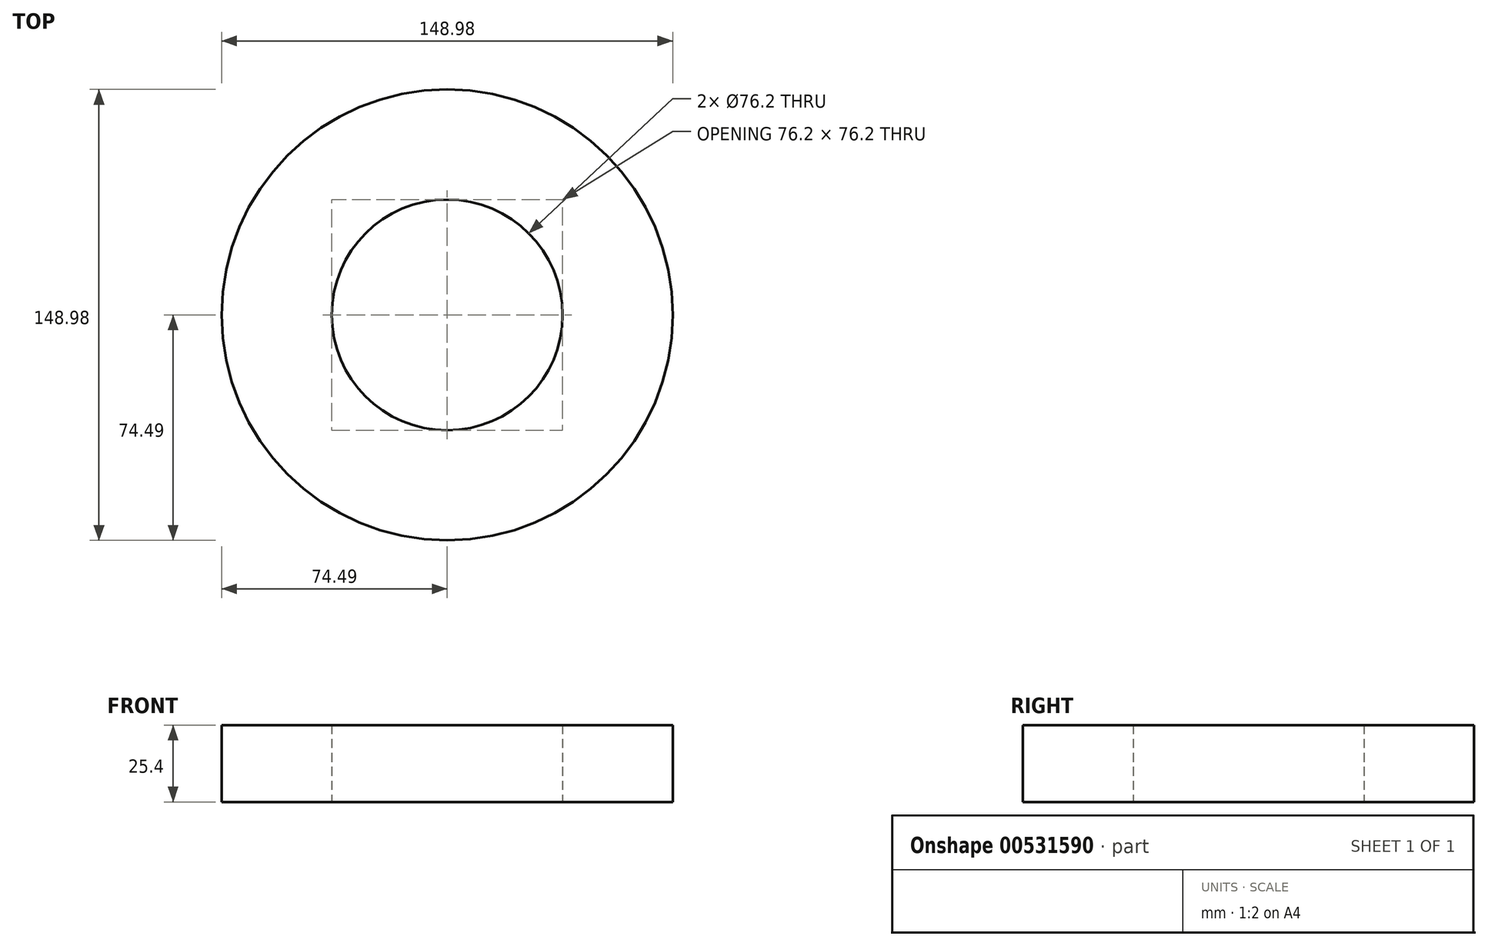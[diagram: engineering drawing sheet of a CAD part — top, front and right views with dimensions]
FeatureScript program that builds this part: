
annotation { "Feature Type Name" : "Feature", "Feature Type Description" : "" }
export const myFeature = defineFeature(function(context is Context, id is Id, definition is map)
    precondition{}
    {
        {
            var Q0;
            Q0=qCreatedBy(makeId("Top.planeOp"),FACE);
            var sketch = newSketch(context, id + "F0", { "sketchPlane" : qUnion([Q0])});
            skCircle(sketch, "E0", {"center": v(0, 0) * mm, "radius": 74.49 * mm});
            skSolve(sketch);
        }
        {
            var Q0;
            Q0=qCreatedBy(makeId("Top.planeOp"),FACE);
            var sketch = newSketch(context, id + "F1", { "sketchPlane" : qUnion([Q0])});
            skCircle(sketch, "E1", {"center": v(0, 0) * mm, "radius": 29.5 * mm});
            skSolve(sketch);
        }
        {
            var Q0;
            Q0 = qSketchRegion(id + "F0", true);
            extrude(context, id + "F2", {"entities" : qUnion([Q0]), "depth" : 25.4 * mm, "offsetDistance" : 25.4 * mm});
        }
        {
            var Q0;
            Q0=sQuery(id+"F1.wireOp",VERTEX,"E1.center");
            var Q1;
            Q1=makeQuery(id+"F2.opExtrude","SWEPT_BODY",BODY,{"disambiguationData":[OSD([sQuery(id+"F0.wireOp",EDGE,"E0")])]});
            hole(context, id + "F3", {"style" : HoleStyle.SIMPLE, "endStyle" : HoleEndStyle.THROUGH, "oppositeDirection" : true, "holeDiameter" : 76.2 * mm, "isTappedThrough" : true, "tappedDepth" : 12.7 * mm, "tapClearance" : 3, "locations" : qUnion([Q0]), "scope" : qUnion([Q1])});
        }
    });
